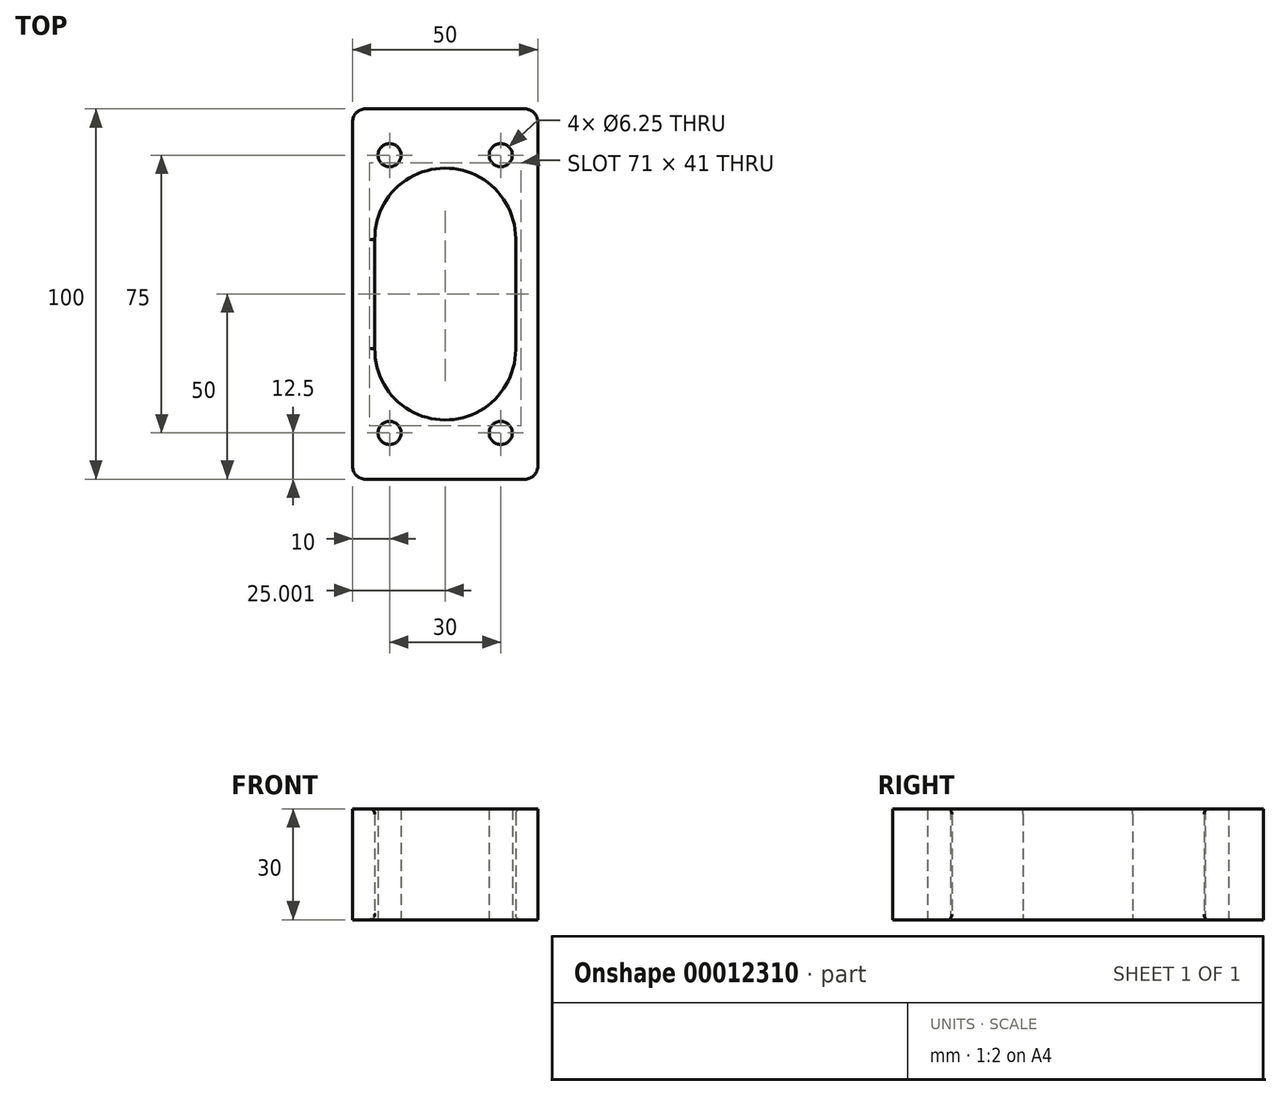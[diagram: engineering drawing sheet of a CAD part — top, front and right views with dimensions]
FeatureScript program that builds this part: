
annotation { "Feature Type Name" : "Feature", "Feature Type Description" : "" }
export const myFeature = defineFeature(function(context is Context, id is Id, definition is map)
    precondition{}
    {
        {
            var Q0;
            Q0=qCreatedBy(makeId("Top.planeOp"),FACE);
            var sketch = newSketch(context, id + "F0", { "sketchPlane" : qUnion([Q0])});
            skLineSegment(sketch, "E0", {"start": v(-3.5, 100) * mm, "end": v(-46.5, 100) * mm});
            skLineSegment(sketch, "E1", {"start": v(-50, 96.5) * mm, "end": v(-50, 3.5) * mm});
            skLineSegment(sketch, "E2", {"start": v(-46.5, 0) * mm, "end": v(-3.5, 0) * mm});
            skCircle(sketch, "E3", {"center": v(-10, 12.5) * mm, "radius": 3.13 * mm});
            skCircle(sketch, "E4", {"center": v(-40, 87.5) * mm, "radius": 3.13 * mm});
            skPoint(sketch, "E5.visualSharp", {"position": v(-50, 100) * mm});
            skPoint(sketch, "E6.visualSharp", {"position": v(-50, 0) * mm});
            skPoint(sketch, "E7.visualSharp", {"position": v(0, 100) * mm});
            skPoint(sketch, "E8.visualSharp", {"position": v(0, 0) * mm});
            skLineSegment(sketch, "E9", {"start": v(0, 96.5) * mm, "end": v(0, 3.5) * mm});
            skArc(sketch, "E10.trimOffspring", {"start": v(-6, 65) * mm, "mid": v(-25.1, 84) * mm, "end": v(-44, 64.79) * mm});
            skCircle(sketch, "E11", {"center": v(-10, 87.5) * mm, "radius": 3.12 * mm});
            skCircle(sketch, "E12", {"center": v(-40, 12.5) * mm, "radius": 3.12 * mm});
            skArc(sketch, "E13", {"start": v(-44, 35.21) * mm, "mid": v(-25.1, 16) * mm, "end": v(-6, 35) * mm});
            skLineSegment(sketch, "E14", {"start": v(-44, 64.79) * mm, "end": v(-44, 34.79) * mm});
            skLineSegment(sketch, "E15", {"start": v(-6, 65) * mm, "end": v(-6, 35) * mm});
            skPoint(sketch, "E16.center.orphan", {"position": v(-25, 50) * mm});
            skArc(sketch, "E17.filletArc", {"start": v(-46.5, 100) * mm, "mid": v(-48.97, 98.97) * mm, "end": v(-50, 96.5) * mm});
            skArc(sketch, "E18.filletArc", {"start": v(0, 96.5) * mm, "mid": v(-1.03, 98.97) * mm, "end": v(-3.5, 100) * mm});
            skArc(sketch, "E19.filletArc", {"start": v(-3.5, 0) * mm, "mid": v(-1.03, 1.03) * mm, "end": v(0, 3.5) * mm});
            skArc(sketch, "E20.filletArc", {"start": v(-50, 3.5) * mm, "mid": v(-48.97, 1.03) * mm, "end": v(-46.5, 0) * mm});
            skSolve(sketch);
        }
        {
            var Q0;
            Q0=makeQuery(id+"F0.imprint","IMPRINT",FACE,{"disambiguationData":[TD([[makeQuery(id+"F0.imprint","IMPRINT",EDGE,{"derivedFrom":sQuery(id+"F0.wireOp",EDGE,"9238ef22-e116-4759-b055-a47255470380")}),1.0]])]});
            var Q1;
            Q1=makeQuery(id+"F0.imprint","IMPRINT",FACE,{"disambiguationData":[TD([[makeQuery(id+"F0.imprint","IMPRINT",EDGE,{"derivedFrom":sQuery(id+"F0.wireOp",EDGE,"E0")}),1.0]])]});
            extrude(context, id + "F1", {"entities" : qUnion([Q0, Q1]), "endBound" : BoundingType.SYMMETRIC, "depth" : 30 * mm});
        }
        {
            var Q0;
            Q0=makeQuery(id+"F1.opExtrude","CAP_EDGE",EDGE,{"disambiguationData":[OSD([sQuery(id+"F0.wireOp",EDGE,"E10.trimOffspring")])],"isStart":false});
            var Q1;
            Q1=makeQuery(id+"F1.opExtrude","CAP_EDGE",EDGE,{"disambiguationData":[OSD([sQuery(id+"F0.wireOp",EDGE,"E15")])],"isStart":false});
            var Q2;
            Q2=makeQuery(id+"F1.opExtrude","CAP_EDGE",EDGE,{"disambiguationData":[OSD([sQuery(id+"F0.wireOp",EDGE,"E13")])],"isStart":false});
            var Q3;
            Q3=makeQuery(id+"F1.opExtrude","CAP_EDGE",EDGE,{"disambiguationData":[OSD([sQuery(id+"F0.wireOp",EDGE,"E14")])],"isStart":false});
            fillet(context, id + "F2", {"entities" : qUnion([Q0, Q1, Q2, Q3]), "radius" : 1.5 * mm, "tangentPropagation" : true, "allowEdgeOverflow" : false});
        }
        {
            var Q0;
            Q0=makeQuery(id+"F1.opExtrude","CAP_EDGE",EDGE,{"disambiguationData":[OSD([sQuery(id+"F0.wireOp",EDGE,"E13")])],"isStart":true});
            var Q1;
            Q1=makeQuery(id+"F1.opExtrude","CAP_EDGE",EDGE,{"disambiguationData":[OSD([sQuery(id+"F0.wireOp",EDGE,"E14")])],"isStart":true});
            var Q2;
            Q2=makeQuery(id+"F1.opExtrude","CAP_EDGE",EDGE,{"disambiguationData":[OSD([sQuery(id+"F0.wireOp",EDGE,"E10.trimOffspring")])],"isStart":true});
            var Q3;
            Q3=makeQuery(id+"F1.opExtrude","CAP_EDGE",EDGE,{"disambiguationData":[OSD([sQuery(id+"F0.wireOp",EDGE,"E15")])],"isStart":true});
            fillet(context, id + "F3", {"entities" : qUnion([Q0, Q1, Q2, Q3]), "radius" : 1.5 * mm, "tangentPropagation" : true, "allowEdgeOverflow" : false});
        }
    });
